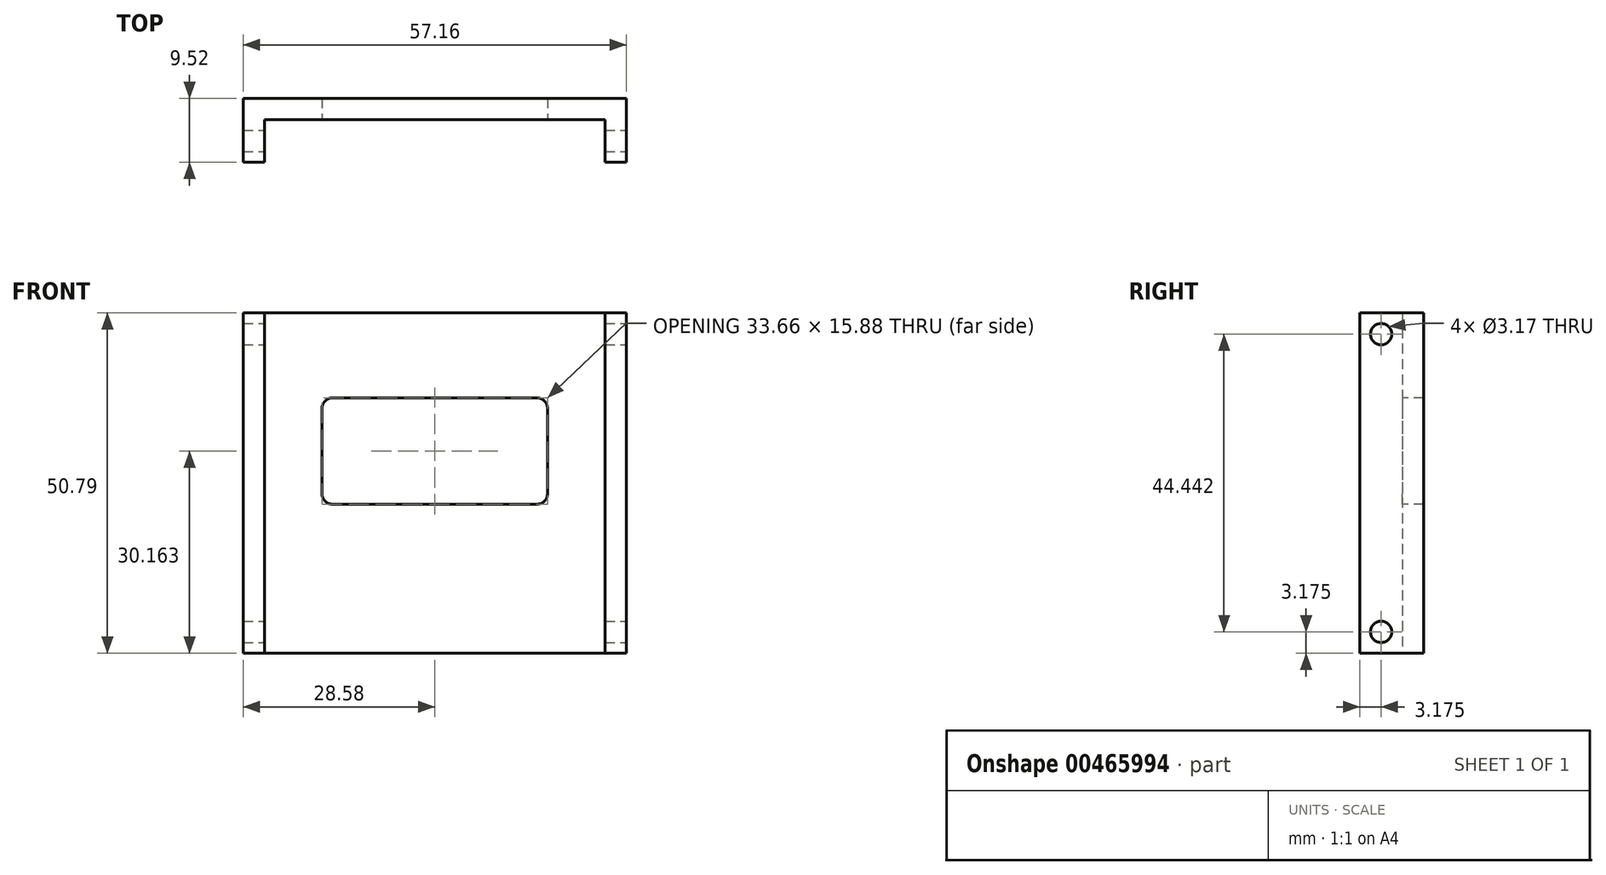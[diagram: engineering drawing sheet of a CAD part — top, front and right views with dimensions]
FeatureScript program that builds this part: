
annotation { "Feature Type Name" : "Feature", "Feature Type Description" : "" }
export const myFeature = defineFeature(function(context is Context, id is Id, definition is map)
    precondition{}
    {
        {
            var Q0;
            Q0=qCreatedBy(makeId("Right.planeOp"),FACE);
            var sketch = newSketch(context, id + "F0", { "sketchPlane" : qUnion([Q0])});
            skLineSegment(sketch, "E0", {"start": v(0, 0) * mm, "end": v(0, 50.8) * mm});
            skLineSegment(sketch, "E1", {"start": v(0, 50.8) * mm, "end": v(3.18, 50.8) * mm});
            skLineSegment(sketch, "E2", {"start": v(3.18, 50.8) * mm, "end": v(3.18, 0) * mm});
            skLineSegment(sketch, "E3", {"start": v(3.18, 0) * mm, "end": v(0, 0) * mm});
            skSolve(sketch);
        }
        {
            var Q0;
            Q0=makeQuery(id+"F0.imprint","IMPRINT",FACE,{"disambiguationData":[TD([[makeQuery(id+"F0.imprint","IMPRINT",EDGE,{"derivedFrom":sQuery(id+"F0.wireOp",EDGE,"E0")}),-1.0]])]});
            extrude(context, id + "F1", {"entities" : qUnion([Q0]), "depth" : 50.8 * mm});
        }
        {
            var Q0;
            Q0=makeQuery(id+"F1.opExtrude","SWEPT_FACE",FACE,{"disambiguationData":[OSD([sQuery(id+"F0.wireOp",EDGE,"E0")])]});
            var sketch = newSketch(context, id + "F2", { "sketchPlane" : qUnion([Q0])});
            skLineSegment(sketch, "E4.bottom", {"start": v(10.16, 38.1) * mm, "end": v(40.64, 38.1) * mm});
            skLineSegment(sketch, "E4.top", {"start": v(10.16, 22.23) * mm, "end": v(40.64, 22.23) * mm});
            skLineSegment(sketch, "E4.left", {"start": v(8.57, 36.51) * mm, "end": v(8.57, 23.81) * mm});
            skLineSegment(sketch, "E4.right", {"start": v(42.23, 36.51) * mm, "end": v(42.23, 23.81) * mm});
            skPoint(sketch, "E5.visualSharp", {"position": v(8.57, 38.1) * mm});
            skArc(sketch, "E5.filletArc", {"start": v(10.16, 38.1) * mm, "mid": v(9.04, 37.64) * mm, "end": v(8.57, 36.51) * mm});
            skPoint(sketch, "E6.visualSharp", {"position": v(8.57, 22.23) * mm});
            skArc(sketch, "E6.filletArc", {"start": v(8.57, 23.81) * mm, "mid": v(9.04, 22.69) * mm, "end": v(10.16, 22.23) * mm});
            skPoint(sketch, "E7.visualSharp", {"position": v(42.23, 22.23) * mm});
            skArc(sketch, "E7.filletArc", {"start": v(40.64, 22.23) * mm, "mid": v(41.76, 22.69) * mm, "end": v(42.23, 23.81) * mm});
            skPoint(sketch, "E8.visualSharp", {"position": v(42.23, 38.1) * mm});
            skArc(sketch, "E8.filletArc", {"start": v(42.23, 36.51) * mm, "mid": v(41.76, 37.64) * mm, "end": v(40.64, 38.1) * mm});
            skSolve(sketch);
        }
        {
            var Q0;
            Q0 = qSketchRegion(id + "F2", true);
            extrude(context, id + "F3", {"entities" : qUnion([Q0]), "operationType" : NewBodyOperationType.REMOVE, "endBound" : BoundingType.THROUGH_ALL, "oppositeDirection" : true, "depth" : 25.4 * mm});
        }
        {
            var Q0;
            Q0=makeQuery(id+"F1.opExtrude","CAP_FACE",FACE,{"disambiguationData":[OSD([sQuery(id+"F0.wireOp",EDGE,"E0"),sQuery(id+"F0.wireOp",EDGE,"E1"),sQuery(id+"F0.wireOp",EDGE,"E2"),sQuery(id+"F0.wireOp",EDGE,"E3")])],"isStart":true});
            extrude(context, id + "F4", {"entities" : qUnion([Q0]), "operationType" : NewBodyOperationType.ADD, "depth" : 3.17 * mm});
        }
        {
            var Q0;
            Q0=makeQuery(id+"F1.opExtrude","CAP_FACE",FACE,{"disambiguationData":[OSD([sQuery(id+"F0.wireOp",EDGE,"E0"),sQuery(id+"F0.wireOp",EDGE,"E1"),sQuery(id+"F0.wireOp",EDGE,"E2"),sQuery(id+"F0.wireOp",EDGE,"E3")])],"isStart":false});
            extrude(context, id + "F5", {"entities" : qUnion([Q0]), "operationType" : NewBodyOperationType.ADD, "depth" : 3.17 * mm});
        }
        {
            var Q0;
            {var subQ0=sQuery(id+"F0.wireOp",EDGE,"E0");Q0=makeQuery(id+"F5.boolean.opBoolean","MERGE",FACE,{"derivedFrom":[makeQuery(id+"F4.boolean.opBoolean","MERGE",FACE,{"derivedFrom":[makeQuery(id+"F1.opExtrude","SWEPT_FACE",FACE,{"disambiguationData":[OSD([subQ0])]}),makeQuery(id+"F4.opExtrude","SWEPT_FACE",FACE,{"disambiguationData":[OSD([subQ0])]})]}),makeQuery(id+"F5.opExtrude","SWEPT_FACE",FACE,{"disambiguationData":[OSD([subQ0])]})]});}
            var sketch = newSketch(context, id + "F6", { "sketchPlane" : qUnion([Q0])});
            skLineSegment(sketch, "E9.bottom", {"start": v(-3.18, 50.8) * mm, "end": v(0, 50.8) * mm});
            skLineSegment(sketch, "E9.top", {"start": v(-3.18, 0) * mm, "end": v(0, 0) * mm});
            skLineSegment(sketch, "E9.left", {"start": v(-3.18, 50.8) * mm, "end": v(-3.18, 0) * mm});
            skLineSegment(sketch, "E9.right", {"start": v(0, 50.8) * mm, "end": v(0, 0) * mm});
            skLineSegment(sketch, "E10.bottom", {"start": v(53.98, 50.8) * mm, "end": v(50.8, 50.8) * mm});
            skLineSegment(sketch, "E10.top", {"start": v(53.98, 0) * mm, "end": v(50.8, 0) * mm});
            skLineSegment(sketch, "E10.left", {"start": v(53.98, 50.8) * mm, "end": v(53.98, 0) * mm});
            skLineSegment(sketch, "E10.right", {"start": v(50.8, 50.8) * mm, "end": v(50.8, 0) * mm});
            skSolve(sketch);
        }
        {
            var Q0;
            Q0 = qSketchRegion(id + "F6", true);
            extrude(context, id + "F7", {"entities" : qUnion([Q0]), "operationType" : NewBodyOperationType.ADD, "depth" : 6.35 * mm});
        }
        {
            var Q0;
            Q0=makeQuery(id+"F7.boolean.opBoolean","MERGE",FACE,{"derivedFrom":[makeQuery(id+"F5.opExtrude","CAP_FACE",FACE,{"disambiguationData":[OSD([sQuery(id+"F0.wireOp",EDGE,"E0"),sQuery(id+"F0.wireOp",EDGE,"E1"),sQuery(id+"F0.wireOp",EDGE,"E2"),sQuery(id+"F0.wireOp",EDGE,"E3")])],"isStart":false}),makeQuery(id+"F7.opExtrude","SWEPT_FACE",FACE,{"disambiguationData":[OSD([sQuery(id+"F6.wireOp",EDGE,"E10.left")])]})]});
            var sketch = newSketch(context, id + "F8", { "sketchPlane" : qUnion([Q0])});
            skCircle(sketch, "E11", {"center": v(-3.18, 47.62) * mm, "radius": 1.59 * mm});
            skCircle(sketch, "E12", {"center": v(-3.18, 3.18) * mm, "radius": 1.59 * mm});
            skSolve(sketch);
        }
        {
            var Q0;
            Q0 = qSketchRegion(id + "F8", true);
            extrude(context, id + "F9", {"entities" : qUnion([Q0]), "operationType" : NewBodyOperationType.REMOVE, "oppositeDirection" : true, "depth" : 63.5 * mm});
        }
    });
